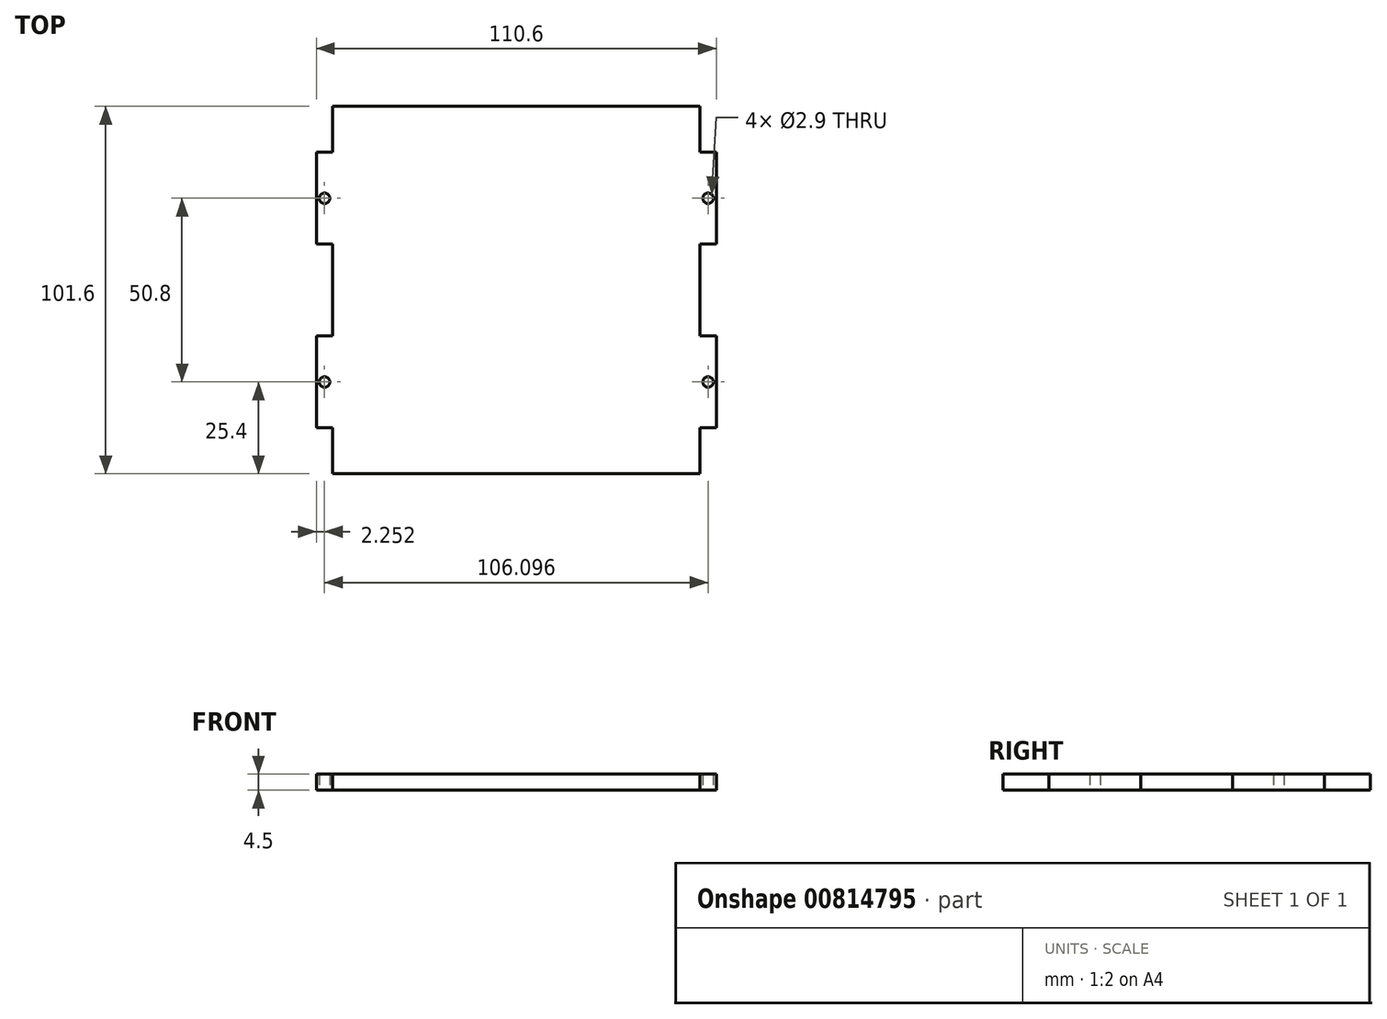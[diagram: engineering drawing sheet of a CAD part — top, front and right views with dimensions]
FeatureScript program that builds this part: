
annotation { "Feature Type Name" : "Feature", "Feature Type Description" : "" }
export const myFeature = defineFeature(function(context is Context, id is Id, definition is map)
    precondition{}
    {
        {
            var Q0;
            Q0=qCreatedBy(makeId("Top.planeOp"),FACE);
            var sketch = newSketch(context, id + "F0", { "sketchPlane" : qUnion([Q0])});
            skLineSegment(sketch, "E0.bottom", {"start": v(-50.8, 50.8) * mm, "end": v(50.8, 50.8) * mm});
            skLineSegment(sketch, "E0.top", {"start": v(-50.8, -50.8) * mm, "end": v(50.8, -50.8) * mm});
            skLineSegment(sketch, "E0.left", {"start": v(-50.8, 50.8) * mm, "end": v(-50.8, 38.1) * mm});
            skLineSegment(sketch, "E1", {"start": v(-50.8, 50.8) * mm, "end": v(50.8, -50.8) * mm, "construction": true});
            skLineSegment(sketch, "E2", {"start": v(-50.8, -50.8) * mm, "end": v(50.8, 50.8) * mm, "construction": true});
            skLineSegment(sketch, "E3", {"start": v(-50.8, 38.1) * mm, "end": v(-55.3, 38.1) * mm});
            skLineSegment(sketch, "E4", {"start": v(-55.3, 38.1) * mm, "end": v(-55.3, 12.7) * mm});
            skLineSegment(sketch, "E5", {"start": v(-55.3, 12.7) * mm, "end": v(-50.8, 12.7) * mm});
            skLineSegment(sketch, "E6", {"start": v(-50.8, 0) * mm, "end": v(50.8, 0) * mm, "construction": true});
            skLineSegment(sketch, "E7", {"start": v(-50.8, 0) * mm, "end": v(-50.8, 12.7) * mm});
            skPoint(sketch, "E8.start.orphan", {"position": v(-50.8, 0) * mm});
            skLineSegment(sketch, "E9.MirrorCS", {"start": v(-50.8, 0) * mm, "end": v(-50.8, -12.7) * mm});
            skLineSegment(sketch, "E10.MirrorCS", {"start": v(-55.3, -12.7) * mm, "end": v(-50.8, -12.7) * mm});
            skLineSegment(sketch, "E11.MirrorCS", {"start": v(-55.3, -38.1) * mm, "end": v(-55.3, -12.7) * mm});
            skLineSegment(sketch, "E12.MirrorCS", {"start": v(-50.8, -38.1) * mm, "end": v(-55.3, -38.1) * mm});
            skLineSegment(sketch, "E13.MirrorCS", {"start": v(-50.8, -50.8) * mm, "end": v(-50.8, -38.1) * mm});
            skCircle(sketch, "E14", {"center": v(-53.05, 25.4) * mm, "radius": 1.45 * mm});
            skLineSegment(sketch, "E15", {"start": v(-55.3, 38.1) * mm, "end": v(-50.8, 12.7) * mm, "construction": true});
            skCircle(sketch, "E16.MirrorC", {"center": v(-53.05, -25.4) * mm, "radius": 1.45 * mm});
            skLineSegment(sketch, "E17", {"start": v(0, 50.8) * mm, "end": v(0, -50.8) * mm, "construction": true});
            skLineSegment(sketch, "E18.MirrorCS", {"start": v(55.3, -12.7) * mm, "end": v(50.8, -12.7) * mm});
            skLineSegment(sketch, "E19.MirrorCS", {"start": v(50.8, -38.1) * mm, "end": v(55.3, -38.1) * mm});
            skLineSegment(sketch, "E20.MirrorCS", {"start": v(55.3, 12.7) * mm, "end": v(50.8, 12.7) * mm});
            skLineSegment(sketch, "E21.MirrorCS", {"start": v(50.8, 38.1) * mm, "end": v(55.3, 38.1) * mm});
            skCircle(sketch, "E22.MirrorC", {"center": v(53.05, 25.4) * mm, "radius": 1.45 * mm});
            skCircle(sketch, "E23.MirrorC", {"center": v(53.05, -25.4) * mm, "radius": 1.45 * mm});
            skLineSegment(sketch, "E24.MirrorCS", {"start": v(55.3, -38.1) * mm, "end": v(55.3, -12.7) * mm});
            skLineSegment(sketch, "E25.MirrorCS", {"start": v(50.8, -50.8) * mm, "end": v(50.8, -38.1) * mm});
            skLineSegment(sketch, "E26.MirrorCS", {"start": v(50.8, 0) * mm, "end": v(50.8, -12.7) * mm});
            skPoint(sketch, "E27.MirrorP", {"position": v(50.8, 0) * mm});
            skLineSegment(sketch, "E28.MirrorCS", {"start": v(50.8, 0) * mm, "end": v(50.8, 12.7) * mm});
            skLineSegment(sketch, "E29.MirrorCS", {"start": v(55.3, 38.1) * mm, "end": v(55.3, 12.7) * mm});
            skLineSegment(sketch, "E30.MirrorCS", {"start": v(50.8, 50.8) * mm, "end": v(50.8, 38.1) * mm});
            skSolve(sketch);
        }
        {
            var Q0;
            Q0 = qSketchRegion(id + "F0", true);
            extrude(context, id + "F1", {"entities" : qUnion([Q0]), "depth" : 4.5 * mm, "offsetDistance" : 25.4 * mm});
        }
    });
